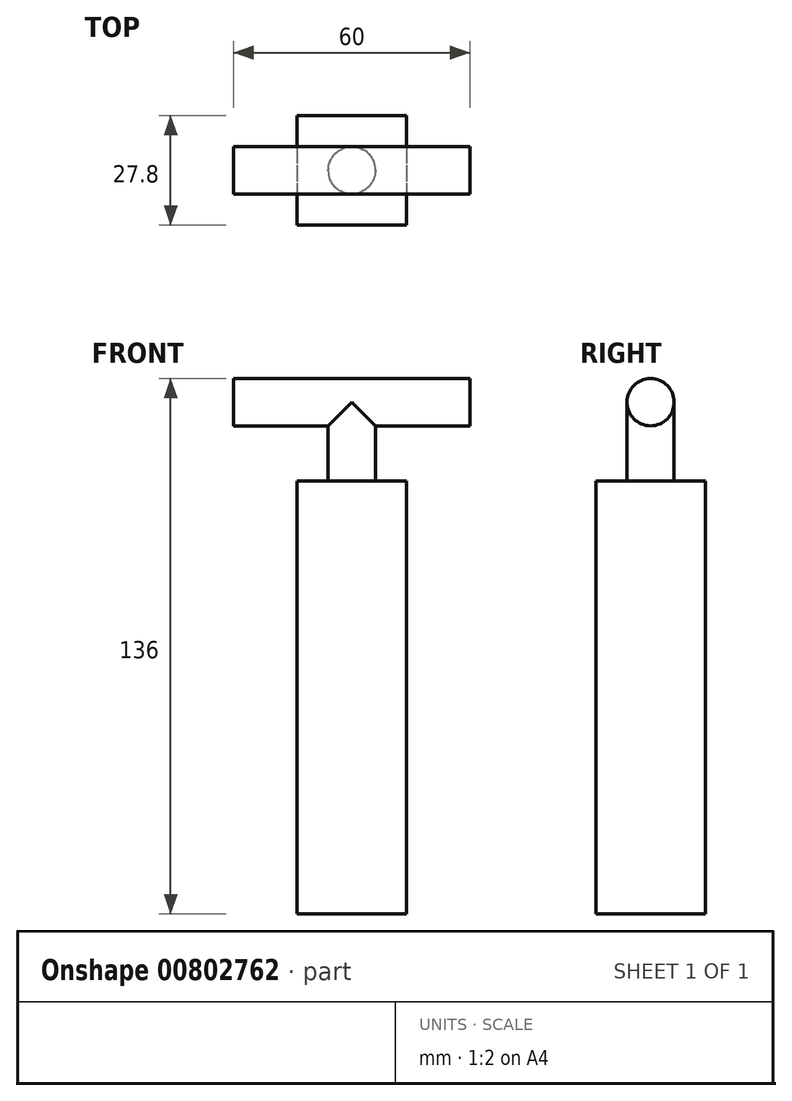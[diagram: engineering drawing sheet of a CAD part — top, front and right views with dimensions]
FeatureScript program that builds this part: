
annotation { "Feature Type Name" : "Feature", "Feature Type Description" : "" }
export const myFeature = defineFeature(function(context is Context, id is Id, definition is map)
    precondition{}
    {
        {
            var Q0;
            Q0=qCreatedBy(makeId("Top.planeOp"),FACE);
            var sketch = newSketch(context, id + "F0", { "sketchPlane" : qUnion([Q0])});
            skLineSegment(sketch, "E0.bottom", {"start": v(13.9, 13.9) * mm, "end": v(-13.9, 13.9) * mm});
            skLineSegment(sketch, "E0.top", {"start": v(13.9, -13.9) * mm, "end": v(-13.9, -13.9) * mm});
            skLineSegment(sketch, "E0.left", {"start": v(13.9, 13.9) * mm, "end": v(13.9, -13.9) * mm});
            skLineSegment(sketch, "E0.right", {"start": v(-13.9, 13.9) * mm, "end": v(-13.9, -13.9) * mm});
            skPoint(sketch, "E0.middle", {"position": v(0, 0) * mm});
            skSolve(sketch);
        }
        {
            var Q0;
            Q0=makeQuery(id+"F0.imprint","IMPRINT",FACE,{"disambiguationData":[TD([[makeQuery(id+"F0.imprint","IMPRINT",EDGE,{"derivedFrom":sQuery(id+"F0.wireOp",EDGE,"E0.bottom")}),1.0]])]});
            extrude(context, id + "F1", {"entities" : qUnion([Q0]), "depth" : 110 * mm, "offsetDistance" : 25 * mm});
        }
        {
            var Q0;
            Q0=makeQuery(id+"F1.opExtrude","CAP_FACE",FACE,{"disambiguationData":[OSD([sQuery(id+"F0.wireOp",EDGE,"E0.bottom"),sQuery(id+"F0.wireOp",EDGE,"E0.top"),sQuery(id+"F0.wireOp",EDGE,"E0.left"),sQuery(id+"F0.wireOp",EDGE,"E0.right")])],"isStart":false});
            var sketch = newSketch(context, id + "F2", { "sketchPlane" : qUnion([Q0])});
            skCircle(sketch, "E1", {"center": v(0, 0) * mm, "radius": 6 * mm});
            skSolve(sketch);
        }
        {
            var Q0;
            Q0=makeQuery(id+"F2.imprint","IMPRINT",FACE,{"disambiguationData":[TD([[makeQuery(id+"F2.imprint","IMPRINT",EDGE,{"derivedFrom":sQuery(id+"F2.wireOp",EDGE,"E1")}),1.0]])]});
            extrude(context, id + "F3", {"entities" : qUnion([Q0]), "operationType" : NewBodyOperationType.ADD, "depth" : 20 * mm, "offsetDistance" : 25 * mm});
        }
        {
            var Q0;
            Q0=qCreatedBy(makeId("Right.planeOp"),FACE);
            var sketch = newSketch(context, id + "F4", { "sketchPlane" : qUnion([Q0])});
            skCircle(sketch, "E2", {"center": v(0, 130) * mm, "radius": 6 * mm});
            skSolve(sketch);
        }
        {
            var Q0;
            Q0 = qSketchRegion(id + "F4", true);
            extrude(context, id + "F5", {"entities" : qUnion([Q0]), "operationType" : NewBodyOperationType.ADD, "endBound" : BoundingType.SYMMETRIC, "depth" : 60 * mm, "offsetDistance" : 25 * mm});
        }
    });
